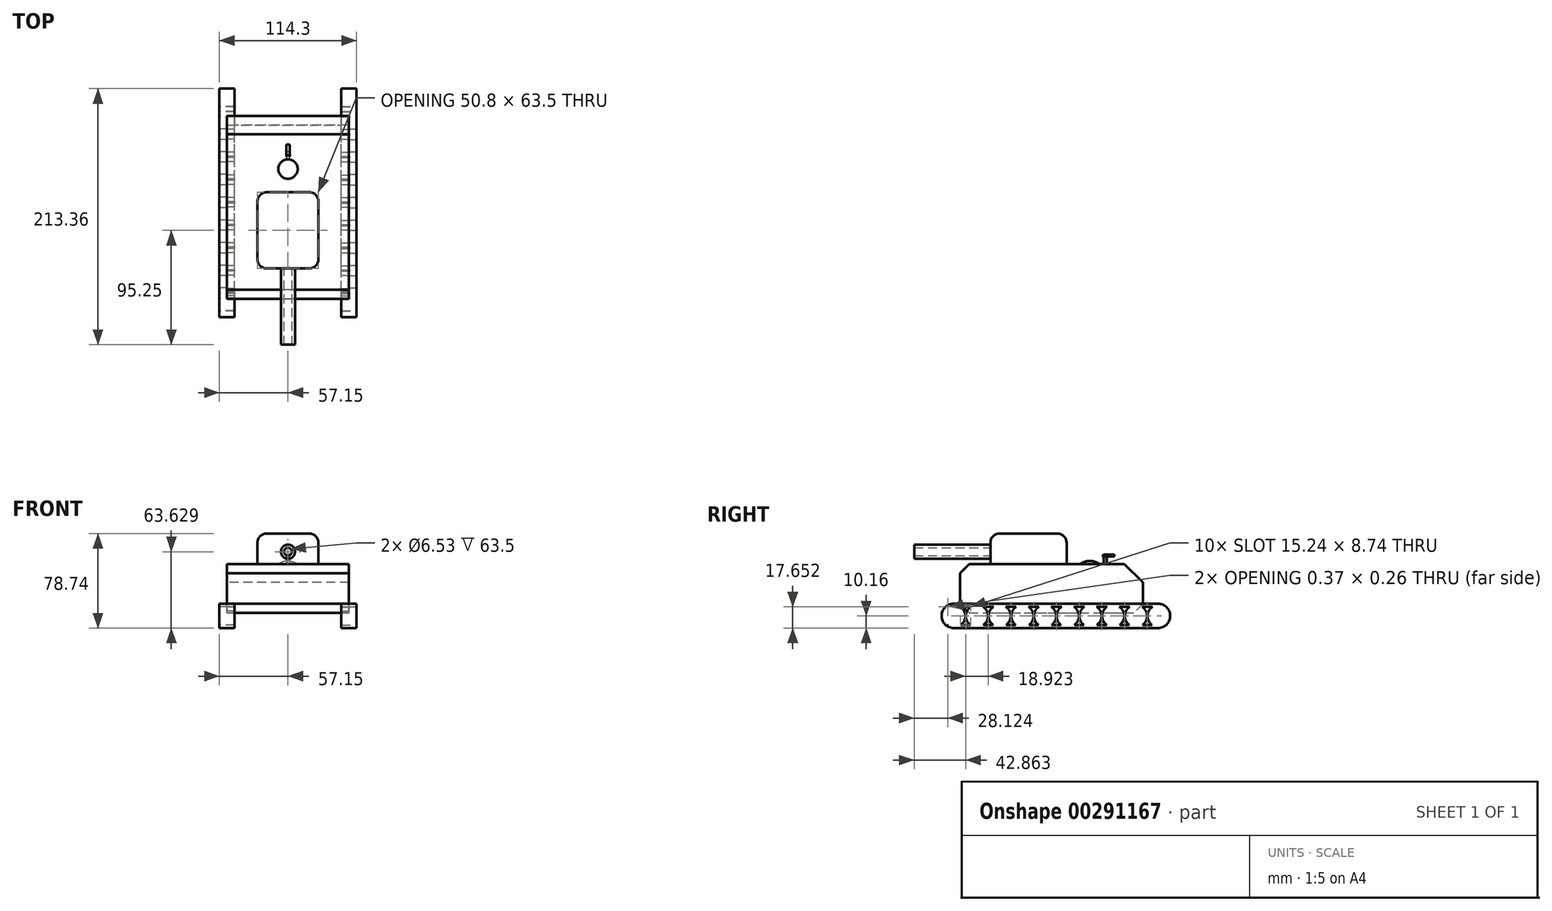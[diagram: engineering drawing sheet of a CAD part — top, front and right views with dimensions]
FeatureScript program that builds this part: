
annotation { "Feature Type Name" : "Feature", "Feature Type Description" : "" }
export const myFeature = defineFeature(function(context is Context, id is Id, definition is map)
    precondition{}
    {
        {
            var Q0;
            Q0=qCreatedBy(makeId("Front.planeOp"),FACE);
            var sketch = newSketch(context, id + "F0", { "sketchPlane" : qUnion([Q0])});
            skLineSegment(sketch, "E0.bottom", {"start": v(-50.8, 0) * mm, "end": v(50.8, 0) * mm});
            skLineSegment(sketch, "E0.top", {"start": v(-50.8, -40.64) * mm, "end": v(50.8, -40.64) * mm});
            skLineSegment(sketch, "E0.left", {"start": v(-50.8, 0) * mm, "end": v(-50.8, -40.64) * mm});
            skLineSegment(sketch, "E0.right", {"start": v(50.8, 0) * mm, "end": v(50.8, -40.64) * mm});
            skSolve(sketch);
        }
        {
            var Q0;
            Q0 = qSketchRegion(id + "F0", true);
            extrude(context, id + "F1", {"entities" : qUnion([Q0]), "depth" : 50.8 * mm, "hasSecondDirection" : true, "secondDirectionOppositeDirection" : true, "secondDirectionDepth" : 101.6 * mm});
        }
        {
            var Q0;
            Q0=qCreatedBy(makeId("Front.planeOp"),FACE);
            var sketch = newSketch(context, id + "F2", { "sketchPlane" : qUnion([Q0])});
            skLineSegment(sketch, "E1.bottom", {"start": v(-25.4, 0) * mm, "end": v(25.4, 0) * mm});
            skLineSegment(sketch, "E1.top", {"start": v(-25.4, 25.4) * mm, "end": v(25.4, 25.4) * mm});
            skLineSegment(sketch, "E1.left", {"start": v(-25.4, 0) * mm, "end": v(-25.4, 25.4) * mm});
            skLineSegment(sketch, "E1.right", {"start": v(25.4, 0) * mm, "end": v(25.4, 25.4) * mm});
            skSolve(sketch);
        }
        {
            var Q0;
            Q0=makeQuery(id+"F2.imprint","IMPRINT",FACE,{"disambiguationData":[TD([[makeQuery(id+"F2.imprint","IMPRINT",EDGE,{"derivedFrom":sQuery(id+"F2.wireOp",EDGE,"E1.bottom")}),1.0]])]});
            extrude(context, id + "F3", {"entities" : qUnion([Q0]), "operationType" : NewBodyOperationType.ADD, "oppositeDirection" : true, "depth" : 38.1 * mm, "hasSecondDirection" : true, "secondDirectionOppositeDirection" : false, "secondDirectionDepth" : 25.4 * mm});
        }
        {
            var Q0;
            Q0=makeQuery(id+"F1.opExtrude","SWEPT_FACE",FACE,{"disambiguationData":[OSD([sQuery(id+"F0.wireOp",EDGE,"E0.right")])]});
            var sketch = newSketch(context, id + "F4", { "sketchPlane" : qUnion([Q0])});
            skLineSegment(sketch, "E2.bottom", {"start": v(-66.04, -33.02) * mm, "end": v(124.46, -33.02) * mm});
            skLineSegment(sketch, "E2.top", {"start": v(-66.04, -53.34) * mm, "end": v(124.46, -53.34) * mm});
            skLineSegment(sketch, "E2.left", {"start": v(-66.04, -33.02) * mm, "end": v(-66.04, -53.34) * mm});
            skLineSegment(sketch, "E2.right", {"start": v(124.46, -33.02) * mm, "end": v(124.46, -53.34) * mm});
            skLineSegment(sketch, "E3.bottom", {"start": v(-60.96, -35.56) * mm, "end": v(119.38, -35.56) * mm});
            skLineSegment(sketch, "E3.top", {"start": v(-60.96, -50.8) * mm, "end": v(119.38, -50.8) * mm});
            skLineSegment(sketch, "E3.left", {"start": v(-60.96, -35.56) * mm, "end": v(-60.96, -50.8) * mm});
            skLineSegment(sketch, "E3.right", {"start": v(119.38, -35.56) * mm, "end": v(119.38, -50.8) * mm});
            skSolve(sketch);
        }
        {
            var Q0;
            Q0=makeQuery(id+"F4.imprint","IMPRINT",FACE,{"disambiguationData":[TD([[makeQuery(id+"F4.imprint","IMPRINT",EDGE,{"derivedFrom":sQuery(id+"F4.wireOp",EDGE,"E2.top")}),1.0]])]});
            var Q1;
            {var subQ0=sQuery(id+"F4.wireOp",EDGE,"E2.bottom");var subQ1=sQuery(id+"F0.wireOp",EDGE,"E0.right");var subQ2=makeQuery(id+"F1.opExtrude","CAP_EDGE",EDGE,{"disambiguationData":[OSD([subQ1])],"isStart":false});var subQ3=makeQuery(id+"F4.imprint","INTERSECT",VERTEX,{"derivedFrom":[subQ2,subQ0]});Q1=makeQuery(id+"F4.imprint","IMPRINT",FACE,{"disambiguationData":[TD([[makeQuery(id+"F4.imprint","IMPRINT",EDGE,{"disambiguationData":[TD([[subQ3,-1.0]])],"derivedFrom":subQ0}),-1.0]])]});}
            extrude(context, id + "F5", {"entities" : qUnion([Q0, Q1]), "operationType" : NewBodyOperationType.ADD, "depth" : 6.35 * mm, "hasSecondDirection" : true, "secondDirectionOppositeDirection" : true, "secondDirectionDepth" : 6.35 * mm});
        }
        {
            var Q0;
            Q0=makeQuery(id+"F5.opExtrude","SWEPT_EDGE",EDGE,{"disambiguationData":[OSD([sQuery(id+"F4.wireOp",EDGE,"E2.top"),sQuery(id+"F4.wireOp",EDGE,"E2.left")])]});
            var Q1;
            Q1=makeQuery(id+"F5.opExtrude","SWEPT_EDGE",EDGE,{"disambiguationData":[OSD([sQuery(id+"F4.wireOp",EDGE,"E2.bottom"),sQuery(id+"F4.wireOp",EDGE,"E2.right")])]});
            var Q2;
            Q2=makeQuery(id+"F5.opExtrude","SWEPT_EDGE",EDGE,{"disambiguationData":[OSD([sQuery(id+"F4.wireOp",EDGE,"E2.top"),sQuery(id+"F4.wireOp",EDGE,"E2.right")])]});
            var Q3;
            Q3=makeQuery(id+"F5.opExtrude","SWEPT_EDGE",EDGE,{"disambiguationData":[OSD([sQuery(id+"F4.wireOp",EDGE,"E2.bottom"),sQuery(id+"F4.wireOp",EDGE,"E2.left")])]});
            fillet(context, id + "F6", {"entities" : qUnion([Q0, Q1, Q2, Q3]), "radius" : 10.16 * mm, "tangentPropagation" : true, "allowEdgeOverflow" : false});
        }
        {
            var Q0;
            Q0=makeQuery(id+"F3.opExtrude","CAP_FACE",FACE,{"disambiguationData":[OSD([sQuery(id+"F2.wireOp",EDGE,"E1.bottom"),sQuery(id+"F2.wireOp",EDGE,"E1.top"),sQuery(id+"F2.wireOp",EDGE,"E1.left"),sQuery(id+"F2.wireOp",EDGE,"E1.right")])],"isStart":true});
            var sketch = newSketch(context, id + "F7", { "sketchPlane" : qUnion([Q0])});
            skCircle(sketch, "E4", {"center": v(0, 10.29) * mm, "radius": 5.84 * mm});
            skCircle(sketch, "E5", {"center": v(0, 10.29) * mm, "radius": 3.26 * mm});
            skSolve(sketch);
        }
        {
            var Q0;
            Q0=makeQuery(id+"F7.imprint","IMPRINT",FACE,{"disambiguationData":[TD([[makeQuery(id+"F7.imprint","IMPRINT",EDGE,{"derivedFrom":sQuery(id+"F7.wireOp",EDGE,"E4")}),1.0]])]});
            extrude(context, id + "F8", {"entities" : qUnion([Q0]), "operationType" : NewBodyOperationType.ADD, "depth" : 63.5 * mm});
        }
        {
            var Q0;
            Q0=makeQuery(id+"F3.opExtrude","CAP_EDGE",EDGE,{"disambiguationData":[OSD([sQuery(id+"F2.wireOp",EDGE,"E1.top")])],"isStart":true});
            var Q1;
            Q1=makeQuery(id+"F3.opExtrude","SWEPT_EDGE",EDGE,{"disambiguationData":[OSD([sQuery(id+"F2.wireOp",EDGE,"E1.top"),sQuery(id+"F2.wireOp",EDGE,"E1.right")])]});
            var Q2;
            Q2=makeQuery(id+"F3.opExtrude","CAP_EDGE",EDGE,{"disambiguationData":[OSD([sQuery(id+"F2.wireOp",EDGE,"E1.top")])],"isStart":false});
            var Q3;
            Q3=makeQuery(id+"F3.opExtrude","SWEPT_EDGE",EDGE,{"disambiguationData":[OSD([sQuery(id+"F2.wireOp",EDGE,"E1.top"),sQuery(id+"F2.wireOp",EDGE,"E1.left")])]});
            var Q4;
            Q4=makeQuery(id+"F3.opExtrude","CAP_EDGE",EDGE,{"disambiguationData":[OSD([sQuery(id+"F2.wireOp",EDGE,"E1.right")])],"isStart":true});
            var Q5;
            Q5=makeQuery(id+"F3.opExtrude","CAP_EDGE",EDGE,{"disambiguationData":[OSD([sQuery(id+"F2.wireOp",EDGE,"E1.left")])],"isStart":true});
            var Q6;
            Q6=makeQuery(id+"F3.opExtrude","CAP_EDGE",EDGE,{"disambiguationData":[OSD([sQuery(id+"F2.wireOp",EDGE,"E1.right")])],"isStart":false});
            var Q7;
            Q7=makeQuery(id+"F3.opExtrude","CAP_EDGE",EDGE,{"disambiguationData":[OSD([sQuery(id+"F2.wireOp",EDGE,"E1.left")])],"isStart":false});
            fillet(context, id + "F9", {"entities" : qUnion([Q0, Q1, Q2, Q3, Q4, Q5, Q6, Q7]), "radius" : 7.62 * mm, "tangentPropagation" : true, "allowEdgeOverflow" : false});
        }
        {
            var Q0;
            Q0=makeQuery(id+"F1.opExtrude","CAP_EDGE",EDGE,{"disambiguationData":[OSD([sQuery(id+"F0.wireOp",EDGE,"E0.bottom")])],"isStart":false});
            var Q1;
            Q1=makeQuery(id+"F1.opExtrude","CAP_EDGE",EDGE,{"disambiguationData":[OSD([sQuery(id+"F0.wireOp",EDGE,"E0.top")])],"isStart":false});
            var Q2;
            Q2=makeQuery(id+"F1.opExtrude","CAP_EDGE",EDGE,{"disambiguationData":[OSD([sQuery(id+"F0.wireOp",EDGE,"E0.top")])],"isStart":true});
            chamfer(context, id + "F10", {"entities" : qUnion([Q0, Q1, Q2]), "width" : 7.62 * mm, "tangentPropagation" : true});
        }
        {
            var Q0;
            Q0=makeQuery(id+"F1.opExtrude","CAP_EDGE",EDGE,{"disambiguationData":[OSD([sQuery(id+"F0.wireOp",EDGE,"E0.bottom")])],"isStart":true});
            chamfer(context, id + "F11", {"entities" : qUnion([Q0]), "width" : 15.24 * mm, "tangentPropagation" : true});
        }
        {
            var Q0;
            Q0=makeQuery(id+"F1.opExtrude","SWEPT_FACE",FACE,{"disambiguationData":[OSD([sQuery(id+"F0.wireOp",EDGE,"E0.bottom")])]});
            var sketch = newSketch(context, id + "F12", { "sketchPlane" : qUnion([Q0])});
            skCircle(sketch, "E6", {"center": v(0, 57.45) * mm, "radius": 8.1 * mm});
            skSolve(sketch);
        }
        {
            var Q0;
            Q0=makeQuery(id+"F12.imprint","IMPRINT",FACE,{"disambiguationData":[TD([[makeQuery(id+"F12.imprint","IMPRINT",EDGE,{"derivedFrom":sQuery(id+"F12.wireOp",EDGE,"E6")}),1.0]])]});
            extrude(context, id + "F13", {"entities" : qUnion([Q0]), "operationType" : NewBodyOperationType.ADD, "depth" : 2.54 * mm});
        }
        {
            var Q0;
            Q0=makeQuery(id+"F13.opExtrude","CAP_EDGE",EDGE,{"disambiguationData":[OSD([sQuery(id+"F12.wireOp",EDGE,"E6")])],"isStart":false});
            fillet(context, id + "F14", {"entities" : qUnion([Q0]), "radius" : 13.97 * mm, "tangentPropagation" : true, "allowEdgeOverflow" : false});
        }
        {
            var Q0;
            Q0=makeQuery(id+"F1.opExtrude","SWEPT_FACE",FACE,{"disambiguationData":[OSD([sQuery(id+"F0.wireOp",EDGE,"E0.bottom")])]});
            var sketch = newSketch(context, id + "F15", { "sketchPlane" : qUnion([Q0])});
            skCircle(sketch, "E7", {"center": v(0, 70.4) * mm, "radius": 1.35 * mm});
            skSolve(sketch);
        }
        {
            var Q0;
            Q0=makeQuery(id+"F15.imprint","IMPRINT",FACE,{"disambiguationData":[TD([[makeQuery(id+"F15.imprint","IMPRINT",EDGE,{"derivedFrom":sQuery(id+"F15.wireOp",EDGE,"E7")}),1.0]])]});
            extrude(context, id + "F16", {"entities" : qUnion([Q0]), "operationType" : NewBodyOperationType.ADD, "depth" : 6.35 * mm});
        }
        {
            var Q0;
            Q0=makeQuery(id+"F5.opExtrude","CAP_FACE",FACE,{"disambiguationData":[OSD([sQuery(id+"F4.wireOp",EDGE,"E2.bottom"),sQuery(id+"F4.wireOp",EDGE,"E2.top"),sQuery(id+"F4.wireOp",EDGE,"E2.left"),sQuery(id+"F4.wireOp",EDGE,"E2.right")])],"isStart":false});
            var sketch = newSketch(context, id + "F17", { "sketchPlane" : qUnion([Q0])});
            skCircle(sketch, "E8", {"center": v(-55.5, -43.3) * mm, "radius": 9.27 * mm});
            skCircle(sketch, "E9.1.0.0", {"center": v(-36.58, -43.3) * mm, "radius": 9.27 * mm});
            skCircle(sketch, "E9.2.0.0", {"center": v(-17.65, -43.3) * mm, "radius": 9.27 * mm});
            skCircle(sketch, "E9.3.0.0", {"center": v(1.27, -43.3) * mm, "radius": 9.27 * mm});
            skCircle(sketch, "E9.4.0.0", {"center": v(20.2, -43.3) * mm, "radius": 9.27 * mm});
            skCircle(sketch, "E9.5.0.0", {"center": v(39.12, -43.3) * mm, "radius": 9.27 * mm});
            skCircle(sketch, "E9.6.0.0", {"center": v(58.04, -43.3) * mm, "radius": 9.27 * mm});
            skCircle(sketch, "E9.7.0.0", {"center": v(76.96, -43.3) * mm, "radius": 9.27 * mm});
            skCircle(sketch, "E9.8.0.0", {"center": v(95.89, -43.3) * mm, "radius": 9.27 * mm});
            skCircle(sketch, "E9.9.0.0", {"center": v(114.8, -43.3) * mm, "radius": 9.27 * mm});
            skLineSegment(sketch, "E9.direction1", {"start": v(-55.5, -43.3) * mm, "end": v(-36.58, -43.3) * mm, "construction": true});
            skSolve(sketch);
        }
        {
            var Q0;
            Q0 = qSketchRegion(id + "F17", true);
            extrude(context, id + "F18", {"entities" : qUnion([Q0]), "operationType" : NewBodyOperationType.ADD, "oppositeDirection" : true, "depth" : 12.7 * mm});
        }
        {
            var Q0;
            Q0=makeQuery(id+"F1.opExtrude","SWEPT_BODY",BODY,{"disambiguationData":[OSD([sQuery(id+"F0.wireOp",EDGE,"E0.bottom"),sQuery(id+"F0.wireOp",EDGE,"E0.top"),sQuery(id+"F0.wireOp",EDGE,"E0.left"),sQuery(id+"F0.wireOp",EDGE,"E0.right")])]});
            var Q1;
            Q1=qCreatedBy(makeId("Right.planeOp"),FACE);
            mirror(context, id + "F19", {"entities" : qUnion([Q0]), "mirrorPlane" : qUnion([Q1])});
        }
        {
            var Q0;
            Q0=makeQuery(id+"F16.opExtrude","CAP_FACE",FACE,{"disambiguationData":[OSD([sQuery(id+"F15.wireOp",EDGE,"E7")])],"isStart":false});
            var sketch = newSketch(context, id + "F20", { "sketchPlane" : qUnion([Q0])});
            skLineSegment(sketch, "E10.bottom", {"start": v(-1.33, 69.08) * mm, "end": v(1.34, 69.08) * mm});
            skLineSegment(sketch, "E10.top", {"start": v(-1.33, 77.97) * mm, "end": v(1.34, 77.97) * mm});
            skLineSegment(sketch, "E10.left", {"start": v(-1.33, 69.08) * mm, "end": v(-1.33, 77.97) * mm});
            skLineSegment(sketch, "E10.right", {"start": v(1.34, 69.08) * mm, "end": v(1.34, 77.97) * mm});
            skSolve(sketch);
        }
        {
            var Q0;
            {var subQ0=sQuery(id+"F20.wireOp",EDGE,"E10.top");Q0=makeQuery(id+"F20.imprint","IMPRINT",FACE,{"disambiguationData":[TD([[makeQuery(id+"F20.imprint","IMPRINT",EDGE,{"derivedFrom":subQ0}),-1.0]])]});}
            var Q1;
            {var subQ0=sQuery(id+"F20.wireOp",EDGE,"E10.right");var subQ1=sQuery(id+"F20.wireOp",EDGE,"E10.bottom");var subQ2=makeQuery(id+"F20.imprint","INTERSECT",VERTEX,{"derivedFrom":[subQ1,subQ0]});Q1=makeQuery(id+"F20.imprint","IMPRINT",FACE,{"disambiguationData":[TD([[makeQuery(id+"F20.imprint","IMPRINT",EDGE,{"disambiguationData":[TD([[subQ2,1.0]])],"derivedFrom":subQ1}),1.0]])]});}
            var Q2;
            {var subQ0=sQuery(id+"F20.wireOp",EDGE,"E10.bottom");var subQ1=makeQuery(id+"F16.opExtrude","CAP_EDGE",EDGE,{"disambiguationData":[OSD([sQuery(id+"F15.wireOp",EDGE,"E7")])],"isStart":false});var subQ2=makeQuery(id+"F20.imprint","INTERSECT",VERTEX,{"disambiguationData":[OD(0.0)],"derivedFrom":[subQ1,subQ0]});Q2=makeQuery(id+"F20.imprint","IMPRINT",FACE,{"disambiguationData":[TD([[makeQuery(id+"F20.imprint","IMPRINT",EDGE,{"disambiguationData":[TD([[subQ2,-1.0]])],"derivedFrom":subQ0}),1.0]])]});}
            var Q3;
            {var subQ0=sQuery(id+"F20.wireOp",EDGE,"E10.left");var subQ1=sQuery(id+"F20.wireOp",EDGE,"E10.bottom");var subQ2=makeQuery(id+"F20.imprint","INTERSECT",VERTEX,{"derivedFrom":[subQ1,subQ0]});Q3=makeQuery(id+"F20.imprint","IMPRINT",FACE,{"disambiguationData":[TD([[makeQuery(id+"F20.imprint","IMPRINT",EDGE,{"disambiguationData":[TD([[subQ2,-1.0]])],"derivedFrom":subQ1}),1.0]])]});}
            extrude(context, id + "F21", {"entities" : qUnion([Q0, Q1, Q2, Q3]), "depth" : 1.52 * mm});
        }
        {
            var Q0;
            Q0=makeQuery(id+"F21.opExtrude","SWEPT_FACE",FACE,{"disambiguationData":[OSD([sQuery(id+"F20.wireOp",EDGE,"E10.right")])]});
            var sketch = newSketch(context, id + "F22", { "sketchPlane" : qUnion([Q0])});
            skLineSegment(sketch, "E11", {"start": v(69.08, 6.35) * mm, "end": v(67.8, 6.35) * mm});
            skLineSegment(sketch, "E12", {"start": v(67.8, 6.35) * mm, "end": v(69.08, 7.87) * mm});
            skPoint(sketch, "E13.oppositeSnap0", {"position": v(68.44, 6.35) * mm});
            skLineSegment(sketch, "E13.bottom", {"start": v(67.8, 6.35) * mm, "end": v(68.44, 6.35) * mm});
            skLineSegment(sketch, "E13.top", {"start": v(67.8, 4.55) * mm, "end": v(68.44, 4.55) * mm});
            skLineSegment(sketch, "E13.left", {"start": v(67.8, 6.35) * mm, "end": v(67.8, 4.55) * mm});
            skLineSegment(sketch, "E13.right", {"start": v(68.44, 6.35) * mm, "end": v(68.44, 4.55) * mm});
            skSolve(sketch);
        }
        {
            var Q0;
            Q0=makeQuery(id+"F22.imprint","IMPRINT",FACE,{"disambiguationData":[TD([[makeQuery(id+"F22.imprint","IMPRINT",EDGE,{"derivedFrom":sQuery(id+"F22.wireOp",EDGE,"E11")}),-1.0]])]});
            var Q1;
            Q1=makeQuery(id+"F22.imprint","IMPRINT",FACE,{"disambiguationData":[TD([[makeQuery(id+"F22.imprint","IMPRINT",EDGE,{"derivedFrom":sQuery(id+"F22.wireOp",EDGE,"E13.bottom")}),-1.0]])]});
            extrude(context, id + "F23", {"entities" : qUnion([Q0, Q1]), "operationType" : NewBodyOperationType.ADD, "oppositeDirection" : true, "depth" : 0.5 * mm});
        }
        {
            var Q0;
            Q0=makeQuery(id+"F21.opExtrude","SWEPT_BODY",BODY,{"disambiguationData":[OSD([sQuery(id+"F20.wireOp",EDGE,"E10.bottom"),sQuery(id+"F20.wireOp",EDGE,"E10.top"),sQuery(id+"F20.wireOp",EDGE,"E10.left"),sQuery(id+"F20.wireOp",EDGE,"E10.right")])]});
            var Q1;
            Q1=qCreatedBy(makeId("Right.planeOp"),FACE);
            mirror(context, id + "F24", {"entities" : qUnion([Q0]), "mirrorPlane" : qUnion([Q1])});
        }
    });
